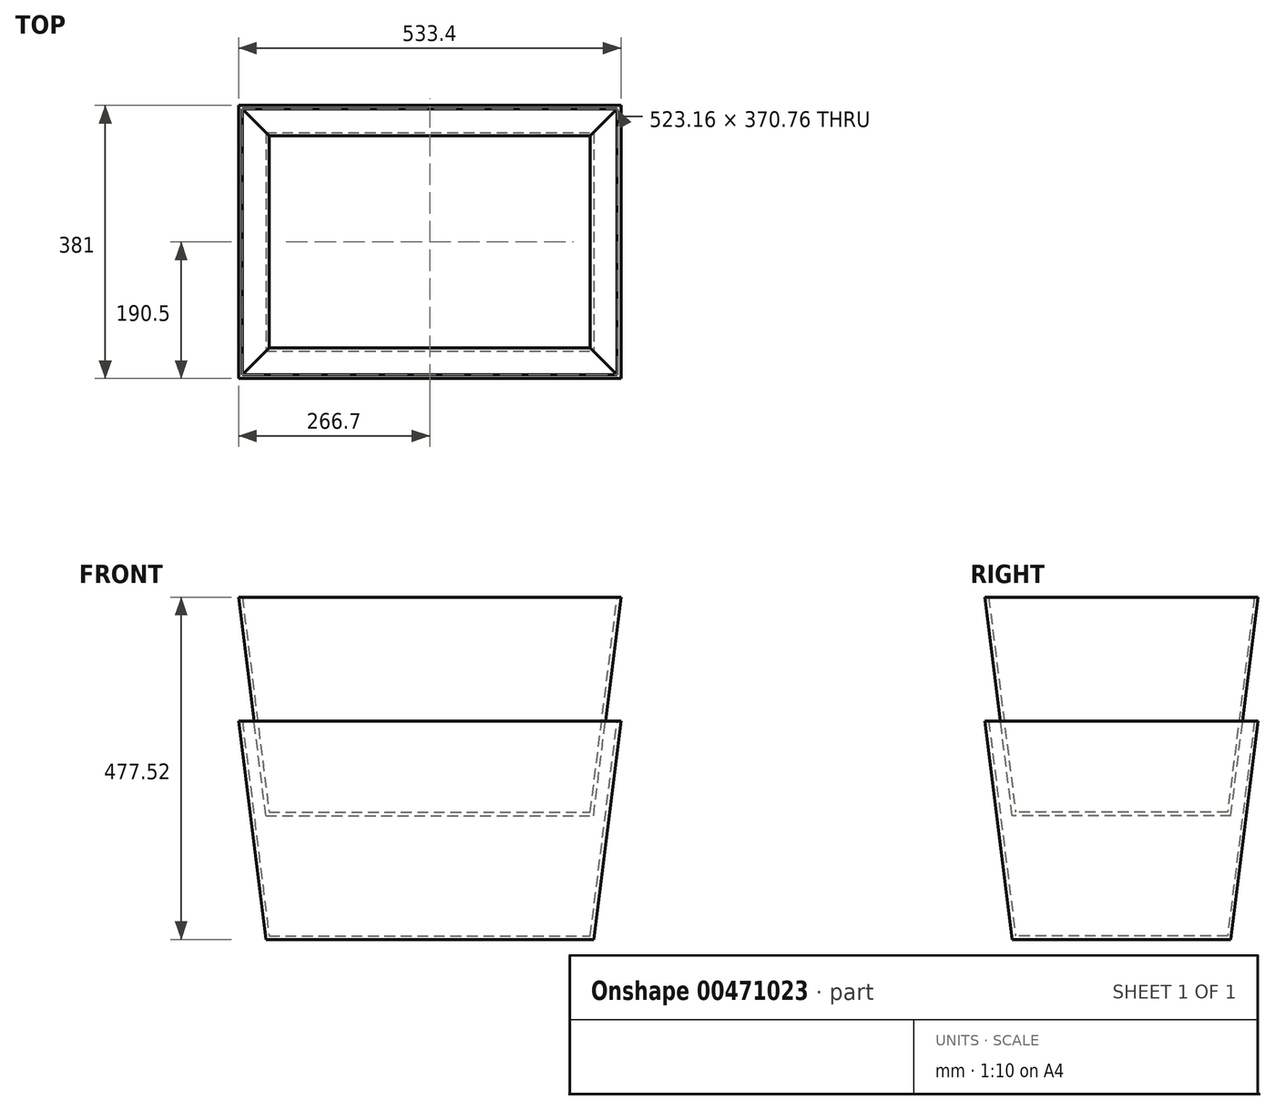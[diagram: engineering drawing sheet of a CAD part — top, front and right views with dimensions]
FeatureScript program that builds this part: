
annotation { "Feature Type Name" : "Feature", "Feature Type Description" : "" }
export const myFeature = defineFeature(function(context is Context, id is Id, definition is map)
    precondition{}
    {
        {
            var Q0;
            Q0=qCreatedBy(makeId("Top.planeOp"),FACE);
            var sketch = newSketch(context, id + "F0", { "sketchPlane" : qUnion([Q0])});
            skLineSegment(sketch, "E0.bottom", {"start": v(-228.6, 152.4) * mm, "end": v(228.6, 152.4) * mm});
            skLineSegment(sketch, "E0.top", {"start": v(-228.6, -152.4) * mm, "end": v(228.6, -152.4) * mm});
            skLineSegment(sketch, "E0.left", {"start": v(-228.6, 152.4) * mm, "end": v(-228.6, -152.4) * mm});
            skLineSegment(sketch, "E0.right", {"start": v(228.6, 152.4) * mm, "end": v(228.6, -152.4) * mm});
            skPoint(sketch, "E0.middle", {"position": v(0, 0) * mm});
            skSolve(sketch);
        }
        {
            var Q0;
            Q0=makeQuery(id+"F0.imprint","IMPRINT",FACE,{"disambiguationData":[TD([[makeQuery(id+"F0.imprint","IMPRINT",EDGE,{"derivedFrom":sQuery(id+"F0.wireOp",EDGE,"E0.bottom")}),-1.0]])]});
            cPlane(context, id + "F1", {"entities" : qUnion([Q0]), "cplaneType" : CPlaneType.OFFSET, "offset" : 304.8 * mm, "width" : 152.4 * mm, "height" : 152.4 * mm});
        }
        {
            var Q0;
            Q0=qCreatedBy(id+"F1.planeOp",FACE);
            var sketch = newSketch(context, id + "F2", { "sketchPlane" : qUnion([Q0])});
            skLineSegment(sketch, "E1.bottom", {"start": v(266.7, 190.5) * mm, "end": v(-266.7, 190.5) * mm});
            skLineSegment(sketch, "E1.top", {"start": v(266.7, -190.5) * mm, "end": v(-266.7, -190.5) * mm});
            skLineSegment(sketch, "E1.left", {"start": v(266.7, 190.5) * mm, "end": v(266.7, -190.5) * mm});
            skLineSegment(sketch, "E1.right", {"start": v(-266.7, 190.5) * mm, "end": v(-266.7, -190.5) * mm});
            skPoint(sketch, "E1.middle", {"position": v(0, 0) * mm});
            skSolve(sketch);
        }
        {
            var Q0;
            Q0=makeQuery(id+"F0.imprint","IMPRINT",FACE,{"disambiguationData":[TD([[makeQuery(id+"F0.imprint","IMPRINT",EDGE,{"derivedFrom":sQuery(id+"F0.wireOp",EDGE,"E0.bottom")}),-1.0]])]});
            var Q1;
            Q1=makeQuery(id+"F2.imprint","IMPRINT",FACE,{"disambiguationData":[TD([[makeQuery(id+"F2.imprint","IMPRINT",EDGE,{"derivedFrom":sQuery(id+"F2.wireOp",EDGE,"E1.bottom")}),1.0]])]});
            loft(context, id + "F3", {"sheetProfilesArray" : [{ "sheetProfileEntities" : qUnion([Q0]) }, { "sheetProfileEntities" : qUnion([Q1]) }]});
        }
        {
            var Q0;
            Q0=makeQuery(id+"F3.opLoft","CAP_FACE",FACE,{"disambiguationData":[OSD([makeQuery(id+"F2.imprint","IMPRINT",FACE,{"disambiguationData":[TD([[makeQuery(id+"F2.imprint","IMPRINT",EDGE,{"derivedFrom":sQuery(id+"F2.wireOp",EDGE,"E1.bottom")}),1.0]])]})])],"isStart":true});
            shell(context, id + "F4", {"entities" : qUnion([Q0]), "thickness" : 5.08 * mm});
        }
        {
            var Q0;
            Q0=makeQuery(id+"F3.opLoft","SWEPT_BODY",BODY,{"disambiguationData":[OSD([makeQuery(id+"F0.imprint","IMPRINT",FACE,{"disambiguationData":[TD([[makeQuery(id+"F0.imprint","IMPRINT",EDGE,{"derivedFrom":sQuery(id+"F0.wireOp",EDGE,"E0.bottom")}),-1.0]])]}),makeQuery(id+"F2.imprint","IMPRINT",FACE,{"disambiguationData":[TD([[makeQuery(id+"F2.imprint","IMPRINT",EDGE,{"derivedFrom":sQuery(id+"F2.wireOp",EDGE,"E1.bottom")}),1.0]])]})])]});
            transform(context, id + "F5", {"entities" : qUnion([Q0]), "transformType" : TransformType.TRANSLATION_3D, "dx" : 0 * mm, "dy" : 0 * mm, "dz" : 172.72 * mm, "makeCopy" : true});
        }
    });
